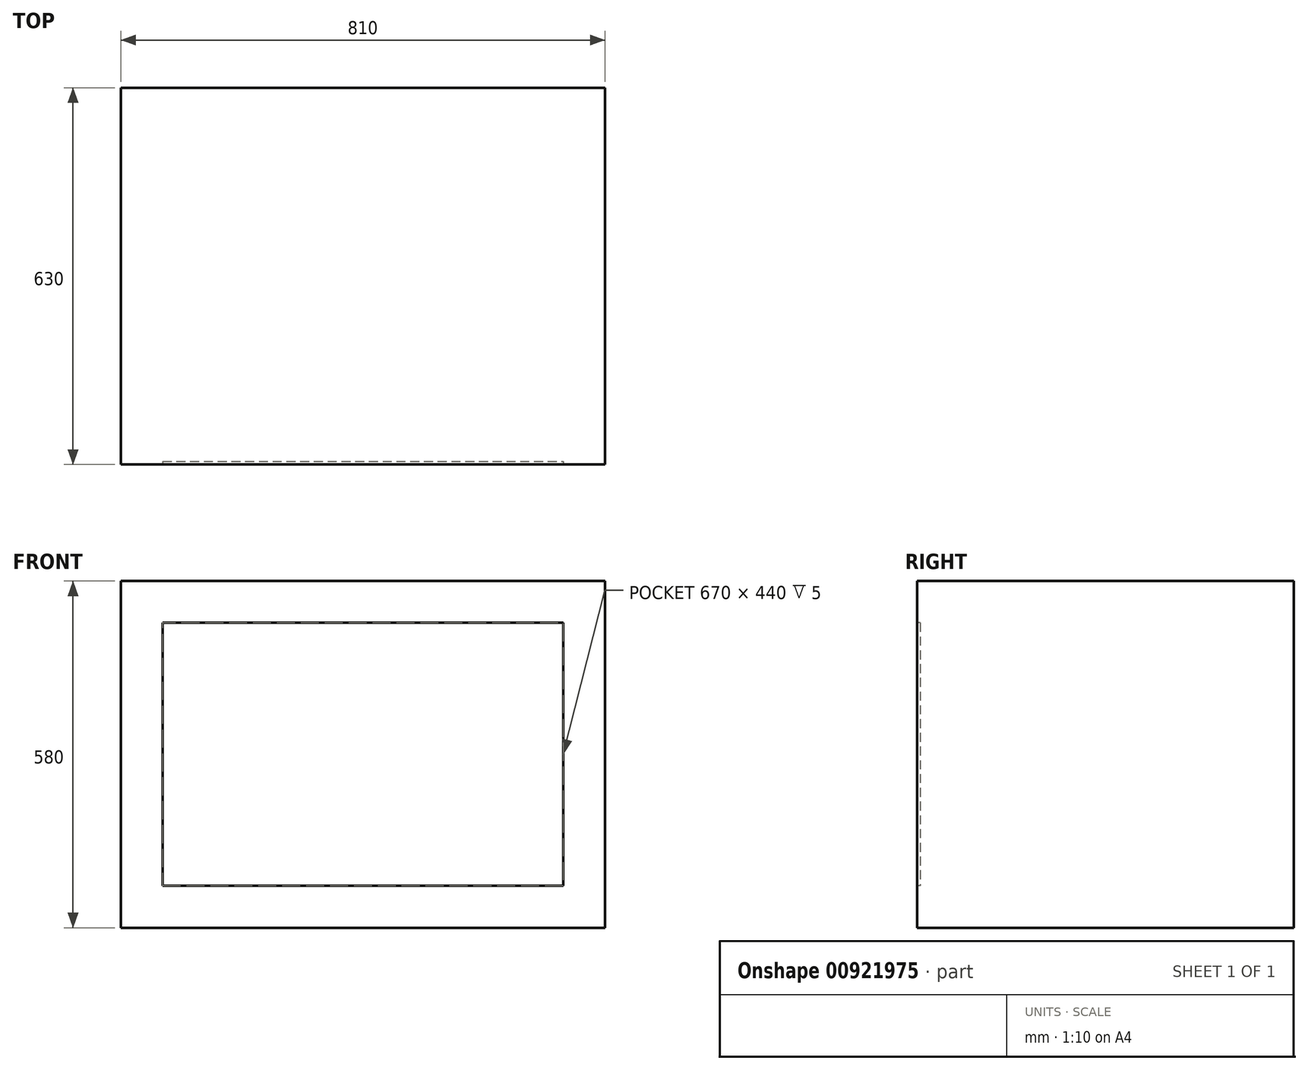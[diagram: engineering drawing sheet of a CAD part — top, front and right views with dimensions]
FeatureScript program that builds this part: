
annotation { "Feature Type Name" : "Feature", "Feature Type Description" : "" }
export const myFeature = defineFeature(function(context is Context, id is Id, definition is map)
    precondition{}
    {
        {
            var Q0;
            Q0=qCreatedBy(makeId("Top.planeOp"),FACE);
            var sketch = newSketch(context, id + "F0", { "sketchPlane" : qUnion([Q0])});
            skLineSegment(sketch, "E0.bottom", {"start": v(405, 315) * mm, "end": v(-405, 315) * mm});
            skLineSegment(sketch, "E0.top", {"start": v(405, -315) * mm, "end": v(-405, -315) * mm});
            skLineSegment(sketch, "E0.left", {"start": v(405, 315) * mm, "end": v(405, -315) * mm});
            skLineSegment(sketch, "E0.right", {"start": v(-405, 315) * mm, "end": v(-405, -315) * mm});
            skPoint(sketch, "E0.middle", {"position": v(0, 0) * mm});
            skSolve(sketch);
        }
        {
            var Q0;
            Q0=makeQuery(id+"F0.imprint","IMPRINT",FACE,{"disambiguationData":[TD([[makeQuery(id+"F0.imprint","IMPRINT",EDGE,{"derivedFrom":sQuery(id+"F0.wireOp",EDGE,"E0.bottom")}),1.0]])]});
            extrude(context, id + "F1", {"entities" : qUnion([Q0]), "depth" : 580 * mm, "offsetDistance" : 25 * mm});
        }
        {
            var Q0;
            Q0=makeQuery(id+"F1.opExtrude","SWEPT_FACE",FACE,{"disambiguationData":[OSD([sQuery(id+"F0.wireOp",EDGE,"E0.top")])]});
            var sketch = newSketch(context, id + "F2", { "sketchPlane" : qUnion([Q0])});
            skLineSegment(sketch, "E1.0", {"start": v(-335, 70) * mm, "end": v(335, 70) * mm});
            skLineSegment(sketch, "E1.1", {"start": v(-335, 510) * mm, "end": v(-335, 70) * mm});
            skLineSegment(sketch, "E1.2", {"start": v(335, 510) * mm, "end": v(-335, 510) * mm});
            skLineSegment(sketch, "E1.3", {"start": v(335, 70) * mm, "end": v(335, 510) * mm});
            skSolve(sketch);
        }
        {
            var Q0;
            Q0=makeQuery(id+"F2.imprint","IMPRINT",FACE,{"disambiguationData":[TD([[makeQuery(id+"F2.imprint","IMPRINT",EDGE,{"derivedFrom":sQuery(id+"F2.wireOp",EDGE,"E1.0")}),1.0]])]});
            extrude(context, id + "F3", {"entities" : qUnion([Q0]), "operationType" : NewBodyOperationType.REMOVE, "oppositeDirection" : true, "depth" : 5 * mm, "offsetDistance" : 25 * mm});
        }
        {
            var Q0;
            Q0=makeQuery(id+"F1.opExtrude","SWEPT_FACE",FACE,{"disambiguationData":[OSD([sQuery(id+"F0.wireOp",EDGE,"E0.bottom")])]});
            var sketch = newSketch(context, id + "F4", { "sketchPlane" : qUnion([Q0])});
            skLineSegment(sketch, "E2.bottom", {"start": v(-1605, 1600) * mm, "end": v(-405, 1600) * mm});
            skLineSegment(sketch, "E2.top", {"start": v(-1605, -400) * mm, "end": v(-405, -400) * mm});
            skLineSegment(sketch, "E2.left", {"start": v(-1605, 1600) * mm, "end": v(-1605, -400) * mm});
            skLineSegment(sketch, "E2.right", {"start": v(-405, 1600) * mm, "end": v(-405, -400) * mm});
            skPoint(sketch, "E2.middle", {"position": v(-1005, 600) * mm});
            skSolve(sketch);
        }
        {
            var Q0;
            {var subQ3=sQuery(id+"F4.wireOp",EDGE,"E2.bottom");Q0=makeQuery(id+"F4.imprint","IMPRINT",FACE,{"disambiguationData":[TD([[makeQuery(id+"F4.imprint","IMPRINT",EDGE,{"derivedFrom":subQ3}),-1.0]])]});}
            extrude(context, id + "F5", {"entities" : qUnion([Q0]), "oppositeDirection" : true, "depth" : 300 * mm, "offsetDistance" : 25 * mm});
        }
        {
            var Q0;
            Q0=makeQuery(id+"F1.opExtrude","SWEPT_FACE",FACE,{"disambiguationData":[OSD([sQuery(id+"F0.wireOp",EDGE,"E0.bottom")])]});
            var sketch = newSketch(context, id + "F6", { "sketchPlane" : qUnion([Q0])});
            skLineSegment(sketch, "E3.0", {"start": v(405, 580) * mm, "end": v(405, 0) * mm});
            skLineSegment(sketch, "E4.0", {"start": v(-405, 580) * mm, "end": v(405, 580) * mm});
            skLineSegment(sketch, "E5.0", {"start": v(705, 880) * mm, "end": v(705, 0) * mm});
            skLineSegment(sketch, "E5.1", {"start": v(-405, 880) * mm, "end": v(705, 880) * mm});
            skLineSegment(sketch, "E6", {"start": v(-405, 880) * mm, "end": v(-805, 880) * mm});
            skLineSegment(sketch, "E7", {"start": v(-805, 880) * mm, "end": v(-805, -400) * mm});
            skLineSegment(sketch, "E8", {"start": v(-805, -400) * mm, "end": v(-405, -400) * mm});
            skLineSegment(sketch, "E9", {"start": v(-405, -400) * mm, "end": v(-405, 580) * mm});
            skLineSegment(sketch, "E10", {"start": v(705, 0) * mm, "end": v(405, 0) * mm});
            skSolve(sketch);
        }
        {
            var Q0;
            Q0=makeQuery(id+"F6.imprint","IMPRINT",FACE,{"disambiguationData":[TD([[makeQuery(id+"F6.imprint","IMPRINT",EDGE,{"derivedFrom":sQuery(id+"F6.wireOp",EDGE,"E3.0")}),1.0]])]});
            extrude(context, id + "F7", {"entities" : qUnion([Q0]), "oppositeDirection" : true, "depth" : 600 * mm, "offsetDistance" : 25 * mm});
        }
        {
            var Q0;
            Q0=makeQuery(id+"F7.opExtrude","CAP_FACE",FACE,{"disambiguationData":[OSD([sQuery(id+"F6.wireOp",EDGE,"E3.0"),sQuery(id+"F6.wireOp",EDGE,"E4.0"),sQuery(id+"F6.wireOp",EDGE,"E5.0"),sQuery(id+"F6.wireOp",EDGE,"E5.1"),sQuery(id+"F6.wireOp",EDGE,"E6"),sQuery(id+"F6.wireOp",EDGE,"E7"),sQuery(id+"F6.wireOp",EDGE,"E8"),sQuery(id+"F6.wireOp",EDGE,"E9"),sQuery(id+"F6.wireOp",EDGE,"E10")])],"isStart":true});
            var sketch = newSketch(context, id + "F8", { "sketchPlane" : qUnion([Q0])});
            skLineSegment(sketch, "E11.0", {"start": v(-805, 880) * mm, "end": v(-805, -400) * mm});
            skLineSegment(sketch, "E12.0", {"start": v(-805, 880) * mm, "end": v(-405, 880) * mm});
            skLineSegment(sketch, "E13.0", {"start": v(-405, 880) * mm, "end": v(-405, -400) * mm});
            skLineSegment(sketch, "E14.0", {"start": v(-805, -400) * mm, "end": v(-405, -400) * mm});
            skPoint(sketch, "E15.orphan", {"position": v(-405, 1600) * mm});
            skPoint(sketch, "E16.orphan", {"position": v(705, 880) * mm});
            skSolve(sketch);
        }
        {
            var Q0;
            Q0=makeQuery(id+"F8.imprint","IMPRINT",FACE,{"disambiguationData":[TD([[makeQuery(id+"F8.imprint","IMPRINT",EDGE,{"derivedFrom":sQuery(id+"F8.wireOp",EDGE,"E11.0")}),1.0]])]});
            extrude(context, id + "F9", {"entities" : qUnion([Q0]), "operationType" : NewBodyOperationType.REMOVE, "oppositeDirection" : true, "depth" : 300 * mm, "offsetDistance" : 25 * mm});
        }
        {
            var Q0;
            Q0=makeQuery(id+"F1.opExtrude","SWEPT_FACE",FACE,{"disambiguationData":[OSD([sQuery(id+"F0.wireOp",EDGE,"E0.bottom")])]});
            var sketch = newSketch(context, id + "F10", { "sketchPlane" : qUnion([Q0])});
            skLineSegment(sketch, "E17.bottom", {"start": v(-405, -80) * mm, "end": v(1105, -80) * mm});
            skLineSegment(sketch, "E17.top", {"start": v(-405, 0) * mm, "end": v(1105, 0) * mm});
            skLineSegment(sketch, "E17.left", {"start": v(-405, -80) * mm, "end": v(-405, 0) * mm});
            skLineSegment(sketch, "E17.right", {"start": v(1105, -80) * mm, "end": v(1105, 0) * mm});
            skLineSegment(sketch, "E18.bottom", {"start": v(-2005, -80) * mm, "end": v(-405, -80) * mm});
            skLineSegment(sketch, "E18.top", {"start": v(-2005, 0) * mm, "end": v(-405, 0) * mm});
            skLineSegment(sketch, "E18.left", {"start": v(-2005, -80) * mm, "end": v(-2005, 0) * mm});
            skSolve(sketch);
        }
        {
            var Q0;
            Q0=makeQuery(id+"F10.imprint","IMPRINT",FACE,{"disambiguationData":[TD([[makeQuery(id+"F10.imprint","IMPRINT",EDGE,{"derivedFrom":sQuery(id+"F10.wireOp",EDGE,"E17.bottom")}),1.0]])]});
            var Q1;
            Q1=makeQuery(id+"F10.imprint","IMPRINT",FACE,{"disambiguationData":[TD([[makeQuery(id+"F10.imprint","IMPRINT",EDGE,{"derivedFrom":sQuery(id+"F10.wireOp",EDGE,"E18.bottom")}),1.0]])]});
            extrude(context, id + "F11", {"entities" : qUnion([Q0, Q1]), "oppositeDirection" : true, "depth" : 700 * mm, "offsetDistance" : 25 * mm});
        }
        {
            var Q0;
            Q0=makeQuery(id+"F11.opExtrude","SWEPT_BODY",BODY,{"disambiguationData":[OSD([sQuery(id+"F10.wireOp",EDGE,"E17.bottom"),sQuery(id+"F10.wireOp",EDGE,"E17.top"),sQuery(id+"F10.wireOp",EDGE,"E17.right"),sQuery(id+"F10.wireOp",EDGE,"E18.bottom"),sQuery(id+"F10.wireOp",EDGE,"E18.top"),sQuery(id+"F10.wireOp",EDGE,"E18.left")])]});
            var Q1;
            Q1=makeQuery(id+"F7.opExtrude","SWEPT_BODY",BODY,{"disambiguationData":[OSD([sQuery(id+"F6.wireOp",EDGE,"E3.0"),sQuery(id+"F6.wireOp",EDGE,"E4.0"),sQuery(id+"F6.wireOp",EDGE,"E5.0"),sQuery(id+"F6.wireOp",EDGE,"E5.1"),sQuery(id+"F6.wireOp",EDGE,"E6"),sQuery(id+"F6.wireOp",EDGE,"E7"),sQuery(id+"F6.wireOp",EDGE,"E8"),sQuery(id+"F6.wireOp",EDGE,"E9"),sQuery(id+"F6.wireOp",EDGE,"E10")])]});
            var Q2;
            Q2=makeQuery(id+"F5.opExtrude","SWEPT_BODY",BODY,{"disambiguationData":[OSD([sQuery(id+"F4.wireOp",EDGE,"E2.bottom"),sQuery(id+"F4.wireOp",EDGE,"E2.top"),sQuery(id+"F4.wireOp",EDGE,"E2.left"),sQuery(id+"F4.wireOp",EDGE,"E2.right")])]});
            deleteBodies(context, id + "F12", {"entities" : qUnion([Q0, Q1, Q2])});
        }
    });
